# Revit family: NBS_Senator_OffcTbls_Ad-libTablesUK_SoftRectangle-ShroudedLeg
name_source: partatom
category: Furniture
revit_build: Autodesk Revit 2016 (Build: 20151007_0715(x64)
units: mm (PartAtom-declared; Revit-internal decimal feet)

## family parameters
Always vertical = Yes
Cut with Voids When Loaded = No
Room Calculation Point = No
Shared = No
Work Plane-Based = No

## types (2) — shared parameters
AssetType = Moveable
CablePortCoverMaterial = NBS_Concept
Category = Pr_40_50_21_60:Office tables
CodePerformance = BS EN 15372 2008, BS 6396 2008
ColourOptions = Carini walnut, mocha, autumn, strata oak, maple, highland oak, beech, winter oak, hacienda white, white, light grey, denim, clay, bordeaux, lemon sorbet, Formica  fundamentals, polyrey, durion
ColumnMaterial = NBS_Concept
Description = Soft rectangular table with shrouded ‘V’ leg
DurationUnit = year
ExpectedLife = 15
ExposedEdgesOptions = Ply effect edging, silver ply edging
FinishOptions = MFC, MFMDF, laminate
FootHeight = 10 mm  [stored 0.0328084 ft]
FrameMountingMaterial = NBS_Concept
FrameShroudMaterial = NBS_Concept
FramesColourOptions = Black, slate grey, light grey
FramesSupports = V’ leg tables utilise an aluminium ski and top casting with steel columns covered in a technical knitted fabric
IfcExportAs = IfcFurnitureType
IfcExportType = TABLE
IsBuiltIn = No
IsSplitTop = No
ManufacturerName = Senator
ManufacturerURL = www.senator.co.uk
ModelReference = Ad-lib tables soft rectangle UK
NBSCertification = www.nationalbimlibrary.com/cert/unxsh4fg
NBSDescription = Office tables
NBSReference = 45-35-20/340
NominalHeight = 740 mm  [stored 2.42782 ft]
OptionalFeatures = In-table power modules, vertical cable riser
PostHeight = 550 mm
PostMaterial = NBS_Concept
ProductInformation = www.Senator.com/FamilyDocuments/474/Senator_SPEC_2017_%20ADLIB%20Tables_v9%20WEB.pdf
Status = UNSET
SustainabilityPerformance = 99% recycleable
TableTopSupportRailMaterial = NBS_Concept
TechMeshOptions = Black, slate grey
Uniclass2015Code = Pr_40_50_21_60
Uniclass2015Title = Office tables
Uniclass2015Version = Products v1.9
Version = 1
WarrantyDescription = Senator warrants that its manufactured products are free from defects for a period of fifteen years on Senator desking ranges
WarrantyDurationParts = 15
WarrantyDurationUnit = year
WorktopHeight = 740 mm  [stored 2.42782 ft]
WorktopMFMDF = No
WorktopMaterial = NBS_Concept
WorktopMaterialTapedEdge = NBS_Concept
WorktopThickness = 25 mm  [stored 0.082021 ft]
WorktopType = NBS_Senator_OffcTbls_Ad-libTablesUK_SoftRectangleMFC : SoftRectangleMFC
WorktopTypeMFC = NBS_Senator_OffcTbls_Ad-libTablesUK_SoftRectangleMFC : SoftRectangleMFC
WorktopTypeMFMDF = NBS_Senator_OffcTbls_Ad-libTablesUK_SoftRectangleMFMDF : SoftRectangleMFMDF
zero-valued in all types: NumberOfChairs, WorksurfaceArea

## per-type parameters (varying)
| type | BIMObjectName | DimensionsPlanSize | Finish | HasProfileEdge | Name | NominalDepth | NominalLength | NominalWidth | Size | TableTopLength | TableTopWidth | WorktopLaminate | WorktopMFC | WorktopTypeLaminate |
| ALP2212SR | NBS_Senator_OfficeTables_Ad-libTablesUK_SoftRectangle_ALP2212SR | 2200 x 1200  mm | Laminate | Yes | OfficeTables_Ad-libTablesUK_SoftRectangle_ALP2212SR_Senator | 1200 mm  [stored 3.93701 ft] | 2200 mm | 1200 mm  [stored 3.93701 ft] | 2200 x 1200 x 740 mm | 2200 mm | 1200 mm  [stored 3.93701 ft] | Yes | No | NBS_Senator_OffcTbls_Ad-libTablesUK_SoftRectangleMFC : SoftRectangleMFC |
| ALP2414SR | NBS_Senator_OfficeTables_Ad-libTablesUK_SoftRectangle_ALP2414SR | 2400 x 1400  mm | MFC | No | OfficeTables_Ad-libTablesUK_SoftRectangle_ALP2414SR_Senator | 1400 mm  [stored 4.59318 ft] | 2400 mm | 1400 mm  [stored 4.59318 ft] | 2400 x 1400 x 740 mm | 2400 mm | 1400 mm  [stored 4.59318 ft] | No | Yes | NBS_Senator_OffcTbls_Ad-libTablesUK_SoftRectangleLaminate : SoftRectangleLaminate |

note: column(s) folded — value = type name in every type: ModelNumber

note: [stored X ft] marks values corroborated as IEEE doubles in the binary element streams (Revit-internal decimal feet)

## geometry (parser evidence)
native form markers: Sweep x20
no freeform markers — native parametric forms only
